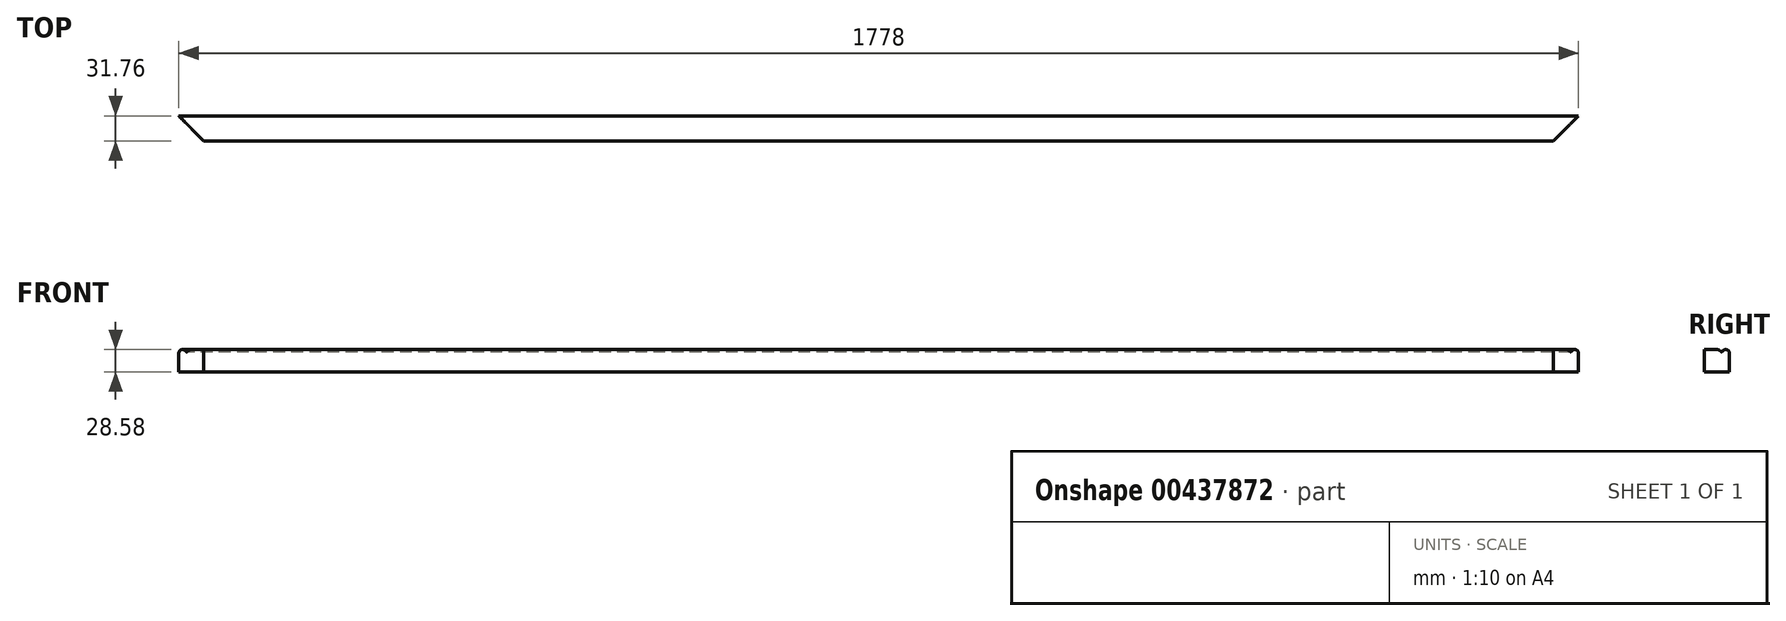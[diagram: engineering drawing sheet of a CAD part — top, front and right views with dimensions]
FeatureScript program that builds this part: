
annotation { "Feature Type Name" : "Feature", "Feature Type Description" : "" }
export const myFeature = defineFeature(function(context is Context, id is Id, definition is map)
    precondition{}
    {
        {
            var Q0;
            Q0=qCreatedBy(makeId("Right.planeOp"),FACE);
            var sketch = newSketch(context, id + "F0", { "sketchPlane" : qUnion([Q0])});
            skLineSegment(sketch, "E0.top", {"start": v(15.88, -14.29) * mm, "end": v(-15.87, -14.29) * mm});
            skLineSegment(sketch, "E0.left", {"start": v(15.88, 9.53) * mm, "end": v(15.88, -14.29) * mm});
            skLineSegment(sketch, "E0.right", {"start": v(-15.88, 14.29) * mm, "end": v(-15.87, -14.29) * mm});
            skArc(sketch, "E1", {"start": v(15.88, 9.53) * mm, "mid": v(12.44, 14.1) * mm, "end": v(7.09, 12.07) * mm});
            skPoint(sketch, "E1.first.point", {"position": v(15.88, 9.53) * mm});
            skPoint(sketch, "E1.second.point", {"position": v(11.11, 14.29) * mm});
            skPoint(sketch, "E1.third.point", {"position": v(7.09, 12.07) * mm});
            skArc(sketch, "E2", {"start": v(4.79, 11.89) * mm, "mid": v(2.38, 13.66) * mm, "end": v(-0.55, 14.29) * mm});
            skPoint(sketch, "E2.first.point", {"position": v(6.45, 8.57) * mm});
            skPoint(sketch, "E2.second.point", {"position": v(-0.55, 14.29) * mm});
            skPoint(sketch, "E2.third.point", {"position": v(-0.55, 0) * mm});
            skArc(sketch, "E3", {"start": v(4.79, 11.89) * mm, "mid": v(5.99, 11.4) * mm, "end": v(7.09, 12.07) * mm});
            skPoint(sketch, "E3.second.point", {"position": v(5.87, 14.29) * mm});
            skPoint(sketch, "E3.third.point", {"position": v(4.79, 11.89) * mm});
            skLineSegment(sketch, "E4.trimOffspring", {"start": v(-0.55, 14.29) * mm, "end": v(-15.88, 14.29) * mm});
            skSolve(sketch);
        }
        {
            var Q0;
            Q0=makeQuery(id+"F0.imprint","IMPRINT",FACE,{"disambiguationData":[TD([[makeQuery(id+"F0.imprint","IMPRINT",EDGE,{"derivedFrom":sQuery(id+"F0.wireOp",EDGE,"E0.top")}),-1.0]])]});
            extrude(context, id + "F1", {"entities" : qUnion([Q0]), "depth" : 1778 * mm, "symmetric" : true});
        }
        {
            var Q0;
            Q0=makeQuery(id+"F1.opExtrude","CAP_EDGE",EDGE,{"disambiguationData":[OSD([sQuery(id+"F0.wireOp",EDGE,"E0.right")])],"isStart":true});
            var Q1;
            Q1=makeQuery(id+"F1.opExtrude","CAP_EDGE",EDGE,{"disambiguationData":[OSD([sQuery(id+"F0.wireOp",EDGE,"E0.right")])],"isStart":false});
            chamfer(context, id + "F2", {"entities" : qUnion([Q0, Q1]), "width" : 31.75 * mm, "tangentPropagation" : true});
        }
    });
